# Revit family: 221010021038299
name_source: partatom
category: Modelos genéricos
revit_build: Autodesk Revit 2018 (Build: 20190510_1515(x64)
units: mm (PartAtom-declared; Revit-internal decimal feet)

## family parameters
Compartido = No
Corte con vacíos al cargar = No
Cota de conector redondo = Diámetro de uso
Puede alojar armadura = No
Punto de cálculo de habitación = No
Se basa en plano de trabajo = No
Siempre vertical = No
Tipo de pieza = Normal

## types (1)
- DECK RAINBODECK HPC 160X25MM CHOCOLATE TIRA 2.2MT
    Alto = 25 mm  [stored 0.082021 ft]
    Aplicacion = Tabla deck Rainbodeck Hpc
    Color = Chocolate
    Descripción = DECK RAINBODECK HPC
    Dimension = 160 mm  [stored 0.524934 ft]
    Empresa = CNP SPA.
    Espesor = 25 mm  [stored 0.082021 ft]
    Largo = 2200 mm
    Material = HPC Chocolate
    Modelo = DECK RAINBODECK HPC
    Nombre SKU = DECK RAINBODECK HPC 160X25MM CHOCOLATE TIRA 2.2MT
    Num SKUs = 221010021038299
    URL = https://www.empresascnp.cl
    Unidad = Tiras de 2.20 Mts
    Url Ficha tecnica = https://empresascnp.cl
    Uso = Producto fabricado en tablas de HPC High Performance Composite, y es una alternativa a la madera tradicional. Debido a su formulación hPC, es un producto innovador, ya que combina la apariencia y nobleza de la madera, con la resistencia y la durabilidad de los polimeros. Siendo un producto de más larga duración y menor mantención.

note: [stored X ft] marks values corroborated as IEEE doubles in the binary element streams (Revit-internal decimal feet)

## geometry (parser evidence)
native form markers: Sweep x2
no freeform markers — native parametric forms only
